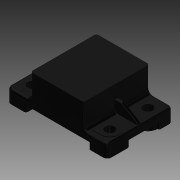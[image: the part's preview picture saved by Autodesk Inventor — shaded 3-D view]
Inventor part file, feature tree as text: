
AUTODESK INVENTOR PART (.ipt)
format: ipt  version: 2018 (Build 220112000, 112)  size: 471,040 bytes
history: native  units: mm (DEFAULTED — no unit token found)
features: sketch x12, extrude x11, fillet x5, mirror x3, plane x2, rib x1
ambient origin geometry x8: Origin, YZ Plane, XZ Plane, XY Plane, X Axis, Y Axis, Z Axis, Center Point
bodies: Solid1 (feature_tree)
feature tree (34):
  extrude  "Extrusion1"  Depth=5.08mm
  fillet  "Fillet19"  Radius=73.66mm
  extrude  "Extrusion4"  Depth=48.26mm TaperAngle=0.0deg
  fillet  "Fillet20"  Radius=3.048mm
  extrude  "Extrusion10"  Depth=1.524mm
  extrude  "Extrusion12"  Depth=10.16mm
  fillet  "Fillet21"  Radius=8.255mm
  plane  "Work Plane3"
  plane  "Work Plane4"
  mirror  "Mirror4"
  mirror  "Mirror5"
  extrude  "Extrusion11"  Depth=0.381mm TaperAngle=0.0deg
  extrude  "Extrusion13"  Depth=3.302mm
  extrude  "Extrusion14"  Depth=8.636mm
  extrude  "Extrusion15"  Depth=2.54mm
  extrude  "Extrusion16"  Depth=0.762mm
  extrude  "Extrusion5"  Depth=3.048mm
  extrude  "Extrusion6"  Depth=13.97mm
  rib  "Rib2"
  fillet  "Fillet22"  Radius=16.51mm
  fillet  "Fillet23"  Radius=4.826mm
  mirror  "Mirror6"
  sketch  "Sketch1"  dims[d1=23.099032mm d2=5.08mm d3=73.66mm]
  sketch  "Sketch5"  dims[d4=38.862mm d5=48.26mm d6=0.0mm d40=3.048mm]
  sketch  "Sketch6"  dims[d41=3.048mm d42=1.524mm]
  sketch  "Sketch7"  dims[d43=6.858mm d44=10.16mm d45=8.255mm]
  sketch  "Sketch8"  dims[d46=8.89mm d47=0.0mm d48=0.381mm d49=0.0mm]
  sketch  "Sketch14"  dims[d50=0.381mm d51=0.0mm d52=3.302mm]
  sketch  "Sketch15"  dims[d53=3.302mm d54=8.636mm]
  sketch  "Sketch16"  dims[d55=3.302mm d56=2.54mm]
  sketch  "Sketch17"  dims[d57=2.54mm d58=0.762mm]
  sketch  "Sketch18"  dims[d59=0.762mm d83=3.048mm]
  sketch  "Sketch19"  dims[d84=1.524mm d85=13.97mm d86=16.51mm d87=4.826mm d88=0.0mm]
  sketch  "Sketch20"  dims[d89=1.27mm d90=4.826mm d91=0.0mm d92=3.048mm d93=1.524mm d94=16.51mm d95=13.97mm d96=4.826mm d97=0.0mm d98=1.27mm d99=4.826mm d100=0.0mm d101=13.97mm d102=13.97mm d103=3.048mm d104=1.524mm d105=1.016mm d106=3.048mm d107=1.524mm d108=1.016mm d109=13.97mm d110=4.826mm d111=0.0mm d112=1.27mm d113=1.27mm d114=0.381mm d116=0.381mm d117=13.97mm d118=4.826mm d119=0.0mm d120=1.27mm d121=0.381mm d122=0.381mm d124=13.97mm d125=4.826mm d126=0.0mm]
